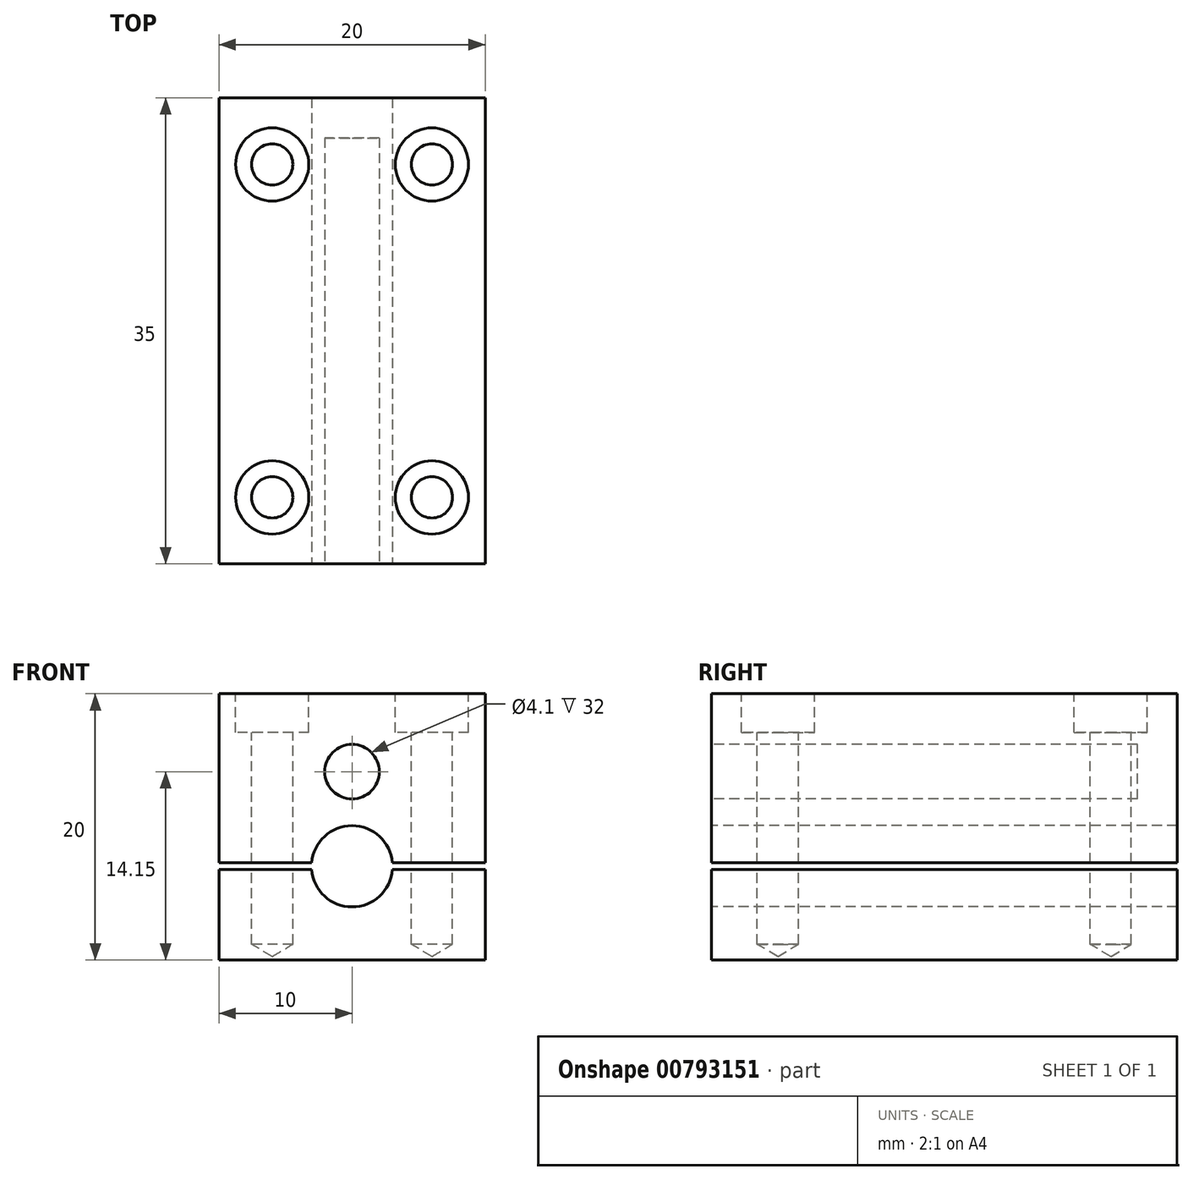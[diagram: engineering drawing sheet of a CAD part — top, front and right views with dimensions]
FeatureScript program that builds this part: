
annotation { "Feature Type Name" : "Feature", "Feature Type Description" : "" }
export const myFeature = defineFeature(function(context is Context, id is Id, definition is map)
    precondition{}
    {
        {
            var Q0;
            Q0=qCreatedBy(makeId("Front.planeOp"),FACE);
            var sketch = newSketch(context, id + "F0", { "sketchPlane" : qUnion([Q0])});
            skLineSegment(sketch, "E0.bottom", {"start": v(10, 10) * mm, "end": v(-10, 10) * mm});
            skLineSegment(sketch, "E0.top", {"start": v(10, -10) * mm, "end": v(-10, -10) * mm});
            skLineSegment(sketch, "E0.left", {"start": v(10, 10) * mm, "end": v(10, -10) * mm});
            skLineSegment(sketch, "E0.right", {"start": v(-10, 10) * mm, "end": v(-10, -10) * mm});
            skPoint(sketch, "E0.middle", {"position": v(0, 0) * mm});
            skCircle(sketch, "E1", {"center": v(0, -2.95) * mm, "radius": 3.05 * mm});
            skCircle(sketch, "E2", {"center": v(0, 4.15) * mm, "radius": 2.05 * mm});
            skPoint(sketch, "E3.middle", {"position": v(0, -8.17) * mm});
            skLineSegment(sketch, "E4.bottom", {"start": v(11, -3.2) * mm, "end": v(-11, -3.2) * mm});
            skLineSegment(sketch, "E4.top", {"start": v(11, -2.7) * mm, "end": v(-11, -2.7) * mm});
            skLineSegment(sketch, "E4.left", {"start": v(11, -3.2) * mm, "end": v(11, -2.7) * mm});
            skLineSegment(sketch, "E4.right", {"start": v(-11, -3.2) * mm, "end": v(-11, -2.7) * mm});
            skSolve(sketch);
        }
        {
            var Q0;
            Q0=makeQuery(id+"F0.imprint","IMPRINT",FACE,{"disambiguationData":[TD([[makeQuery(id+"F0.imprint","IMPRINT",EDGE,{"derivedFrom":sQuery(id+"F0.wireOp",EDGE,"E0.bottom")}),1.0]])]});
            var Q1;
            Q1=makeQuery(id+"F0.imprint","IMPRINT",FACE,{"disambiguationData":[TD([[makeQuery(id+"F0.imprint","IMPRINT",EDGE,{"derivedFrom":sQuery(id+"F0.wireOp",EDGE,"E2")}),1.0]])]});
            var Q2;
            {var subQ5=sQuery(id+"F0.wireOp",EDGE,"E0.top");Q2=makeQuery(id+"F0.imprint","IMPRINT",FACE,{"disambiguationData":[TD([[makeQuery(id+"F0.imprint","IMPRINT",EDGE,{"derivedFrom":subQ5}),-1.0]])]});}
            extrude(context, id + "F1", {"entities" : qUnion([Q0, Q1, Q2]), "oppositeDirection" : true, "depth" : 35 * mm, "offsetDistance" : 25 * mm});
        }
        {
            var Q0;
            Q0=makeQuery(id+"F0.imprint","IMPRINT",FACE,{"disambiguationData":[TD([[makeQuery(id+"F0.imprint","IMPRINT",EDGE,{"derivedFrom":sQuery(id+"F0.wireOp",EDGE,"E2")}),1.0]])]});
            extrude(context, id + "F2", {"entities" : qUnion([Q0]), "operationType" : NewBodyOperationType.REMOVE, "oppositeDirection" : true, "depth" : 32 * mm, "offsetDistance" : 25 * mm});
        }
        {
            var Q0;
            Q0=makeQuery(id+"F1.opExtrude","SWEPT_FACE",FACE,{"disambiguationData":[OSD([sQuery(id+"F0.wireOp",EDGE,"E0.bottom")])]});
            var sketch = newSketch(context, id + "F3", { "sketchPlane" : qUnion([Q0])});
            skPoint(sketch, "E5", {"position": v(-6, 5) * mm});
            skPoint(sketch, "E6.0.1.0", {"position": v(-6, 30) * mm});
            skPoint(sketch, "E6.1.0.0", {"position": v(6, 5) * mm});
            skPoint(sketch, "E6.1.1.0", {"position": v(6, 30) * mm});
            skLineSegment(sketch, "E6.direction1", {"start": v(-6, 5) * mm, "end": v(6, 5) * mm, "construction": true});
            skLineSegment(sketch, "E6.direction2", {"start": v(-6, 5) * mm, "end": v(-6, 30) * mm, "construction": true});
            skSolve(sketch);
        }
        {
            var Q0;
            Q0=sQuery(id+"F3.wireOp",VERTEX,"E6.0.1.0");
            var Q1;
            Q1=sQuery(id+"F3.wireOp",VERTEX,"E6.1.1.0");
            var Q2;
            Q2=sQuery(id+"F3.wireOp",VERTEX,"E5");
            var Q3;
            Q3=sQuery(id+"F3.wireOp",VERTEX,"E6.1.0.0");
            var Q4;
            Q4=makeQuery(id+"F1.opExtrude","SWEPT_BODY",BODY,{"disambiguationData":[OSD([sQuery(id+"F0.wireOp",EDGE,"E0.bottom"),sQuery(id+"F0.wireOp",EDGE,"E0.left"),sQuery(id+"F0.wireOp",EDGE,"E0.right"),sQuery(id+"F0.wireOp",EDGE,"E1"),sQuery(id+"F0.wireOp",EDGE,"E4.top")])]});
            var Q5;
            Q5=makeQuery(id+"F1.opExtrude","SWEPT_BODY",BODY,{"disambiguationData":[OSD([sQuery(id+"F0.wireOp",EDGE,"E0.top"),sQuery(id+"F0.wireOp",EDGE,"E0.left"),sQuery(id+"F0.wireOp",EDGE,"E0.right"),sQuery(id+"F0.wireOp",EDGE,"E1"),sQuery(id+"F0.wireOp",EDGE,"E4.bottom")])]});
            hole(context, id + "F4", {"style" : HoleStyle.C_BORE, "endStyle" : HoleEndStyle.BLIND, "holeDiameter" : 3.1 * mm, "cBoreDiameter" : 5.5 * mm, "cBoreDepth" : 2.9 * mm, "majorDiameter" : 3 * mm, "holeDepth" : 18.8 * mm, "isTappedThrough" : true, "tappedDepth" : 12 * mm, "tapClearance" : 3, "locations" : qUnion([Q0, Q1, Q2, Q3]), "scope" : qUnion([Q4, Q5])});
        }
    });
